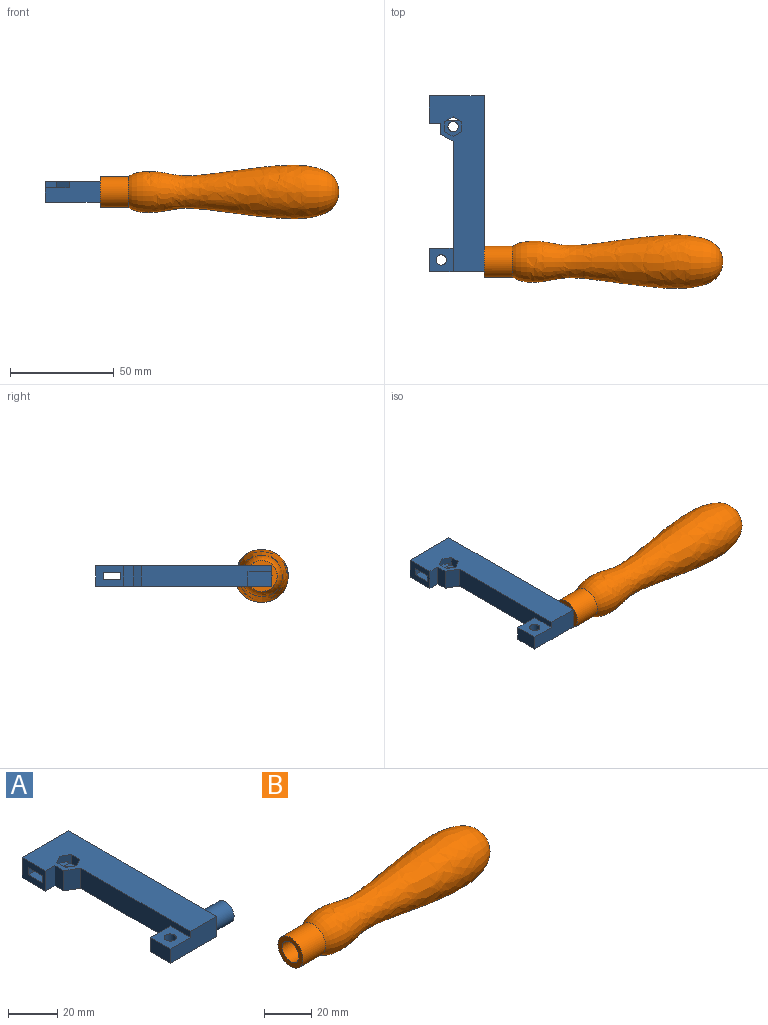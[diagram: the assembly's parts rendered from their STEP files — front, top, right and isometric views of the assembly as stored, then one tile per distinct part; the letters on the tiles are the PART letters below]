
ASSEMBLY  parts=2 mates=1
PART A: 30 faces, bbox 36.5x85x10 mm
  f0: plane 85x26.5mm, normal (0,0,1), area 1413.4mm2, adj f1,f6,f7,f9,f10,f13,f14,f15
  f1: plane 26.5x10mm, normal (0,-1,0), area 230.5mm2, adj f0,f3,f6,f7,f8,f25
  f2: plane 11.5x7mm, normal (0,1,0), area 80.5mm2, adj f3,f6,f8,f25
  f3: plane 11.5x7mm, normal (-1,0,0), area 80.5mm2, adj f1,f2,f8,f25
  f4: plane 26.5x3.5mm, normal (0,1,0), area 80.9mm2, adj f5,f7,f10,f12,f18,f19,f21,f22
  f5: plane 26.5x8.2mm, normal (0,0,-1), area 213mm2, adj f4,f7,f10,f11,f18,f19
  f6: plane 62.96x10mm, normal (-1,0,0), area 549.1mm2, adj f0,f1,f2,f8,f14,f25
  f7: plane 85x10mm, normal (1,0,0), area 745.9mm2, adj f0,f1,f4,f5,f8,f11,f12,f27
  f8: plane 85x26.5mm, normal (0,0,-1), area 1517.8mm2, adj f1,f2,f3,f6,f7,f9,f10,f13
  f9: plane 10x5.4mm, normal (0,-1,0), area 54mm2, adj f0,f8,f10,f13
  f10: plane 13.5x10mm, normal (-1,0,0), area 106.3mm2, adj f0,f4,f5,f8,f9,f11,f12,f29
  f11: plane 26.5x3.5mm, normal (0,-1,0), area 92.8mm2, adj f5,f7,f10,f12
  f12: plane 26.5x8.2mm, normal (0,0,1), area 210.6mm2, adj f4,f7,f10,f11,f22
  f13: plane 10x5.02mm, normal (-1,0,0), area 50.2mm2, adj f0,f8,f9,f14
  f14: plane 10x6.1mm, normal (-0.5,-0.87,0), area 70.4mm2, adj f0,f6,f8,f13
  f15: plane 4.5x4.1mm, normal (0.5,0.87,0), area 21.3mm2, adj f0,f16,f20,f21
  f16: plane 4.5x4.1mm, normal (-0.5,0.87,0), area 21.3mm2, adj f0,f15,f17,f21
  f17: plane 4.73x4.5mm, normal (-1,0,0), area 21.3mm2, adj f0,f16,f18,f21
  f18: plane 4.5x4.1mm, normal (-0.5,-0.87,0), area 17.3mm2, adj f0,f4,f5,f17,f19,f21
  f19: plane 4.5x4.1mm, normal (0.5,-0.87,0), area 17.3mm2, adj f0,f4,f5,f18,f20,f21
  f20: plane 4.73x4.5mm, normal (1,0,0), area 21.3mm2, adj f0,f15,f19,f21
  f21: plane 8.2x7.88mm, normal (0,0,1), area 34.2mm2, adj f4,f15,f16,f17,f18,f19,f20,f24
  f22: cylinder r=4.6mm len=9.2mm, axis (0,0,-1), area 110mm2, adj f4,f8,f12,f23
  f23: plane 9.2x7.75mm, normal (0,0,-1), area 40.1mm2, adj f4,f22,f24
  f24: cylinder r=2.5mm len=5mm, axis (0,0,-1), area 23.6mm2, adj f21,f23
  f25: plane 11.5x11.5mm, normal (0,0,1), area 112.6mm2, adj f1,f2,f3,f6,f26
  f26: cylinder r=2.5mm len=7mm, axis (0,0,1), area 110mm2, adj f8,f25
  f27: cylinder r=4.9mm len=10mm, axis (-1,0,0), area 307.9mm2, adj f7,f28
  f28: plane 9.8x9.8mm, normal (1,0,0), area 75.4mm2, adj f27
  f29: plane 26.5x10mm, normal (0,1,0), area 265mm2, adj f0,f7,f8,f10
PART B: 5 faces, bbox 13.6x15x15 mm
  f0: cylinder r=7.5mm len=15mm, axis (-1,0,0), area 641.8mm2, adj f1,f2
  f1: plane 15x15mm, normal (-1,0,0), area 98.2mm2, adj f0,f3
  f2: revolved ~7.5x7.5mm, area 0mm2, adj f0
  f3: cylinder r=5mm len=10mm, axis (-1,0,0), area 314.2mm2, adj f1,f4
  f4: plane 10x10mm, normal (-1,0,0), area 78.5mm2, adj f3
PLACE A t=(8.51,-29.66,12.54)mm
PLACE B t=(18.51,-24.76,17.54)mm
MATE fastened B.f0 <-> A.f27  axis (-1,0,0) through (18.51,-24.76,17.54)mm
